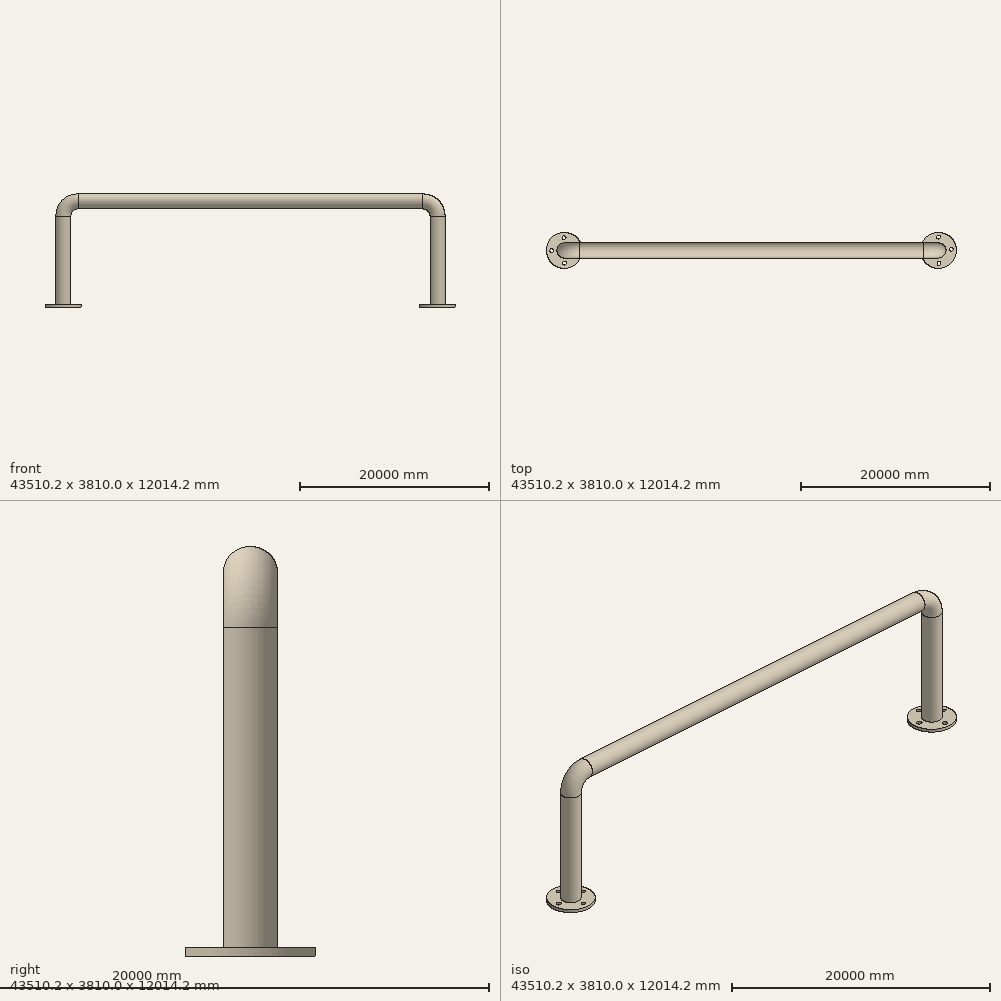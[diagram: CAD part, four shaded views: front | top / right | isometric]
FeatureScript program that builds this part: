
annotation { "Feature Type Name" : "Feature", "Feature Type Description" : "" }
export const myFeature = defineFeature(function(context is Context, id is Id, definition is map)
    precondition{}
    {
        {
            var Q0;
            Q0=qCreatedBy(makeId("Front.planeOp"),FACE);
            var sketch = newSketch(context, id + "F0", { "sketchPlane" : qUnion([Q0])});
            skLineSegment(sketch, "E0", {"start": v(0, 0) * mm, "end": v(0, 9398) * mm});
            skLineSegment(sketch, "E1", {"start": v(762, 10160) * mm, "end": v(37338, 10160) * mm});
            skLineSegment(sketch, "E2", {"start": v(38100, 9398) * mm, "end": v(38100, 0) * mm});
            skPoint(sketch, "E3.visualSharp", {"position": v(0, 10160) * mm});
            skArc(sketch, "E3.filletArc", {"start": v(762, 10160) * mm, "mid": v(223.18, 9936.82) * mm, "end": v(0, 9398) * mm});
            skPoint(sketch, "E4.visualSharp", {"position": v(38100, 10160) * mm});
            skArc(sketch, "E4.filletArc", {"start": v(38100, 9398) * mm, "mid": v(37876.82, 9936.82) * mm, "end": v(37338, 10160) * mm});
            skSolve(sketch);
        }
        {
            var Q0;
            Q0=qCreatedBy(makeId("Top.planeOp"),FACE);
            var sketch = newSketch(context, id + "F1", { "sketchPlane" : qUnion([Q0])});
            skCircle(sketch, "E5", {"center": v(-800.1, 0) * mm, "radius": 800.1 * mm});
            skSolve(sketch);
        }
        {
            var Q0;
            Q0=makeQuery(id+"F1.imprint","IMPRINT",FACE,{"disambiguationData":[TD([[makeQuery(id+"F1.imprint","IMPRINT",EDGE,{"derivedFrom":sQuery(id+"F1.wireOp",EDGE,"E5")}),1.0]])]});
            var Q1;
            Q1=sQuery(id+"F0.wireOp",EDGE,"E1");
            var Q2;
            Q2=sQuery(id+"F0.wireOp",EDGE,"E0");
            var Q3;
            Q3=sQuery(id+"F0.wireOp",EDGE,"E3.filletArc");
            var Q4;
            Q4=sQuery(id+"F0.wireOp",EDGE,"E4.filletArc");
            var Q5;
            Q5=sQuery(id+"F0.wireOp",EDGE,"E2");
            sweep(context, id + "F2", {"profiles" : qUnion([Q0]), "path" : qUnion([Q1, Q2, Q3, Q4, Q5])});
        }
        {
            var Q0;
            Q0=makeQuery(id+"F2.opSweep","CAP_FACE",FACE,{"disambiguationData":[OSD([sQuery(id+"F0.wireOp",VERTEX,"E0.start"),sQuery(id+"F1.wireOp",EDGE,"E5")])],"isStart":true});
            var sketch = newSketch(context, id + "F3", { "sketchPlane" : qUnion([Q0])});
            skCircle(sketch, "E6", {"center": v(-800.1, 0) * mm, "radius": 1905 * mm});
            skCircle(sketch, "E7", {"center": v(38900.1, 0) * mm, "radius": 1905 * mm});
            skCircle(sketch, "E8", {"center": v(-775.3, 1345.97) * mm, "radius": 203.2 * mm});
            skCircle(sketch, "E9.1.0", {"center": v(-2146.07, 24.8) * mm, "radius": 203.2 * mm});
            skCircle(sketch, "E9.2.0", {"center": v(-824.9, -1345.97) * mm, "radius": 203.2 * mm});
            skCircle(sketch, "E9.3.0", {"center": v(545.87, -24.8) * mm, "radius": 203.2 * mm});
            skCircle(sketch, "E10", {"center": v(38947.41, 1390.23) * mm, "radius": 203.2 * mm});
            skCircle(sketch, "E11.1.0", {"center": v(37576.65, -46.38) * mm, "radius": 203.2 * mm});
            skCircle(sketch, "E11.2.0", {"center": v(38897.82, -1417.14) * mm, "radius": 203.2 * mm});
            skCircle(sketch, "E11.3.0", {"center": v(40268.6, -95.97) * mm, "radius": 203.2 * mm});
            skSolve(sketch);
        }
        {
            var Q0;
            Q0 = qSketchRegion(id + "F3", true);
            extrude(context, id + "F4", {"entities" : qUnion([Q0]), "operationType" : NewBodyOperationType.ADD, "depth" : 254 * mm, "offsetDistance" : 25.4 * mm});
        }
    });
